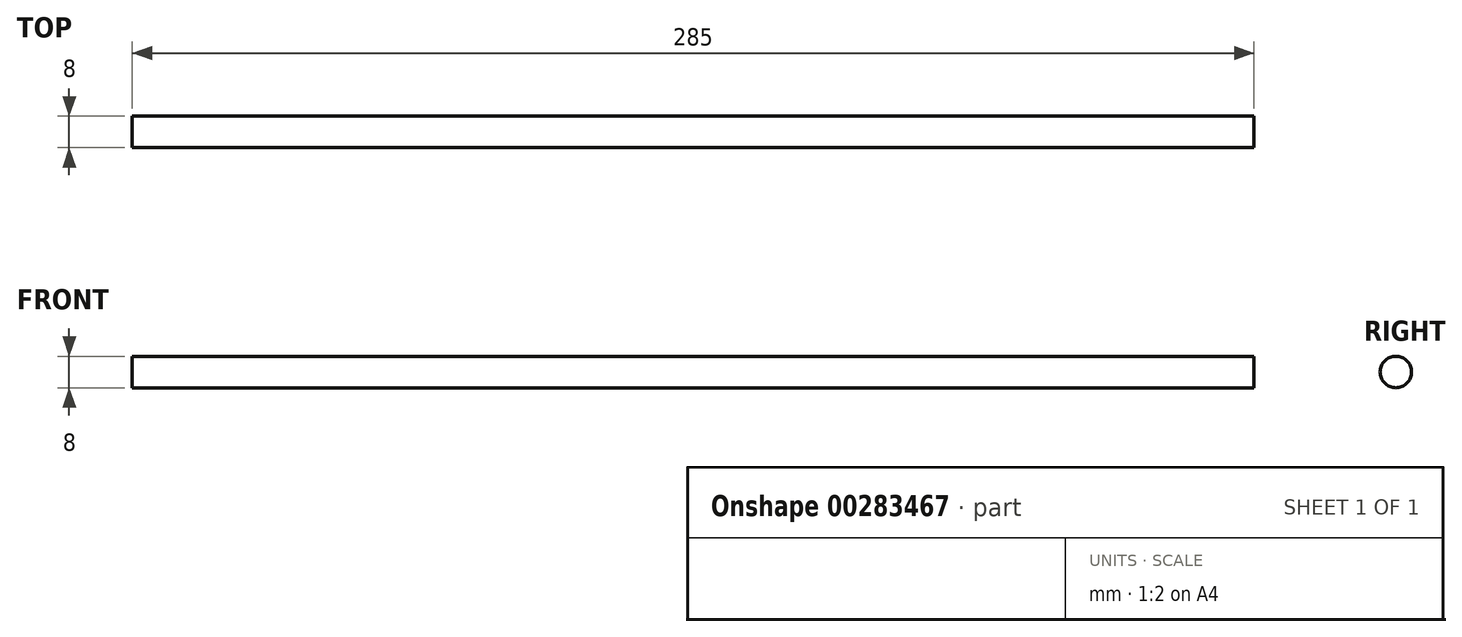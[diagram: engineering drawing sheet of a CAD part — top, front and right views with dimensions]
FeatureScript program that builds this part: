
annotation { "Feature Type Name" : "Feature", "Feature Type Description" : "" }
export const myFeature = defineFeature(function(context is Context, id is Id, definition is map)
    precondition{}
    {
        {
            var Q0;
            Q0=qCreatedBy(makeId("Top.planeOp"),FACE);
            var sketch = newSketch(context, id + "F0", { "sketchPlane" : qUnion([Q0])});
            skLineSegment(sketch, "E0", {"start": v(-142.5, 0) * mm, "end": v(-142.5, 4) * mm});
            skLineSegment(sketch, "E1", {"start": v(-142.5, 4) * mm, "end": v(-50, 4) * mm});
            skLineSegment(sketch, "E2", {"start": v(-50, 4) * mm, "end": v(-50, 4) * mm});
            skLineSegment(sketch, "E3", {"start": v(-50, 4) * mm, "end": v(0, 4) * mm});
            skLineSegment(sketch, "E4", {"start": v(0, -10.3) * mm, "end": v(0, 18.1) * mm, "construction": true});
            skLineSegment(sketch, "E5", {"start": v(-54.75, 0) * mm, "end": v(22.4, 0) * mm, "construction": true});
            skLineSegment(sketch, "E6.MirrorCS", {"start": v(142.5, 0) * mm, "end": v(142.5, 4) * mm});
            skLineSegment(sketch, "E7.MirrorCS", {"start": v(50, 4) * mm, "end": v(50, 4) * mm});
            skLineSegment(sketch, "E8.MirrorCS", {"start": v(142.5, 4) * mm, "end": v(50, 4) * mm});
            skLineSegment(sketch, "E9.MirrorCS", {"start": v(50, 4) * mm, "end": v(0, 4) * mm});
            skLineSegment(sketch, "E10", {"start": v(-142.5, 0) * mm, "end": v(142.5, 0) * mm});
            skSolve(sketch);
        }
        {
            var Q0;
            Q0=makeQuery(id+"F0.imprint","IMPRINT",FACE,{"disambiguationData":[TD([[makeQuery(id+"F0.imprint","IMPRINT",EDGE,{"derivedFrom":sQuery(id+"F0.wireOp",EDGE,"E0")}),-1.0]])]});
            var Q1;
            Q1=sQuery(id+"F0.wireOp",EDGE,"E10");
            revolve(context, id + "F1", {"entities" : qUnion([Q0]), "axis" : qUnion([Q1]), "revolveType" : RevolveType.FULL});
        }
    });
